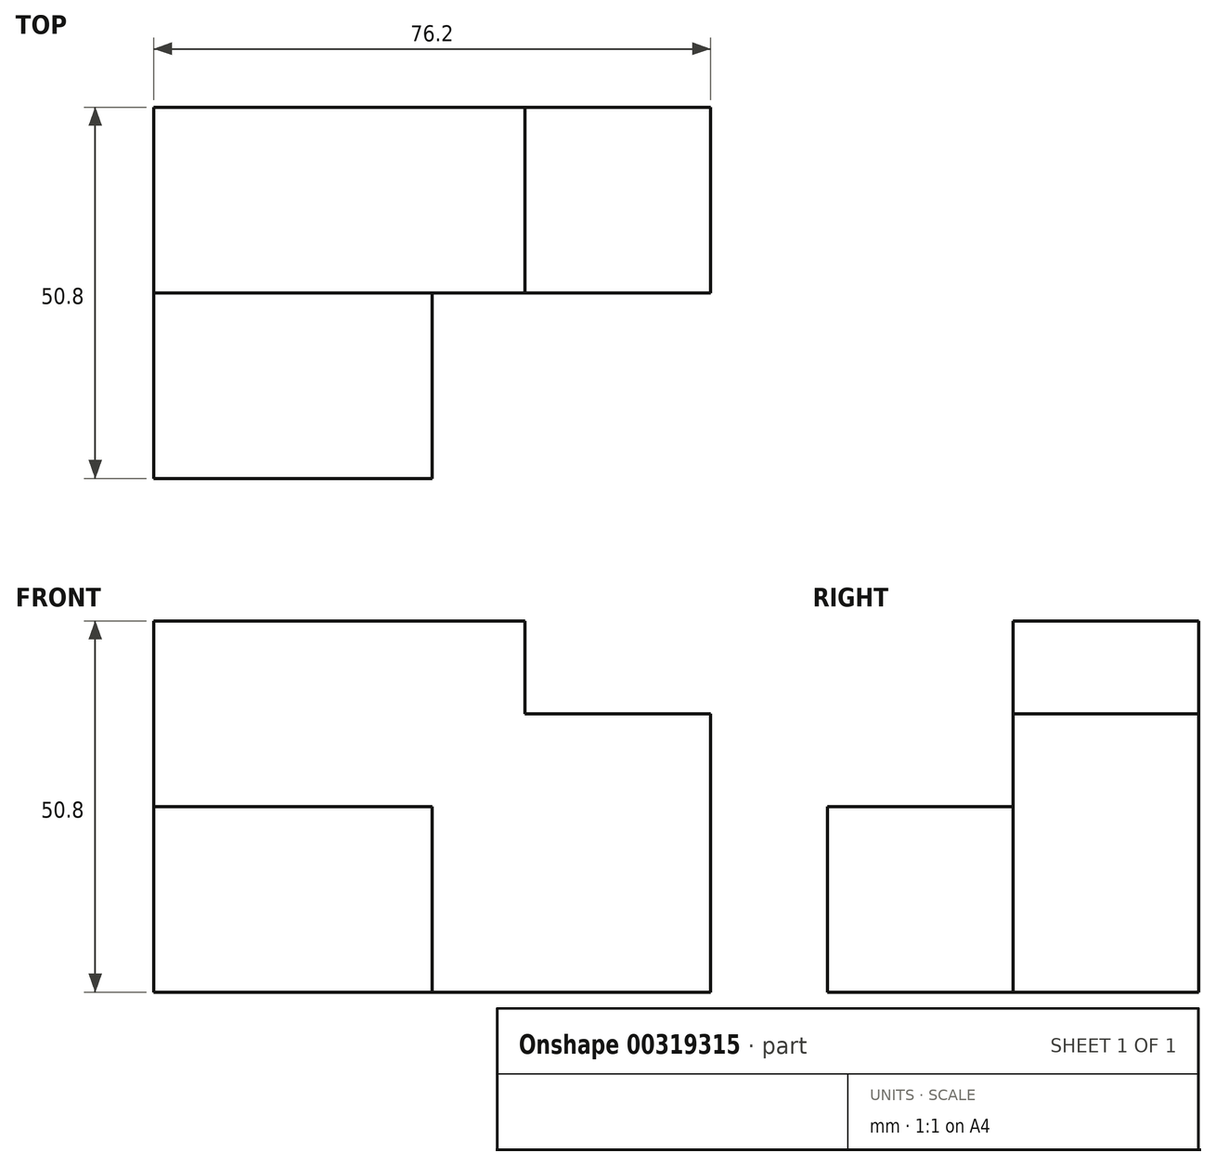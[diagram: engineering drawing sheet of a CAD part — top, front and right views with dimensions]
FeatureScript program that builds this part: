
annotation { "Feature Type Name" : "Feature", "Feature Type Description" : "" }
export const myFeature = defineFeature(function(context is Context, id is Id, definition is map)
    precondition{}
    {
        {
            var Q0;
            Q0=qCreatedBy(makeId("Top.planeOp"),FACE);
            var sketch = newSketch(context, id + "F0", { "sketchPlane" : qUnion([Q0])});
            skLineSegment(sketch, "E0", {"start": v(-44.14, -25.57) * mm, "end": v(32.06, -25.57) * mm});
            skLineSegment(sketch, "E1", {"start": v(32.06, -25.57) * mm, "end": v(32.06, -0.17) * mm});
            skLineSegment(sketch, "E2", {"start": v(32.06, -0.17) * mm, "end": v(-44.14, -0.17) * mm});
            skLineSegment(sketch, "E3", {"start": v(-44.14, -0.17) * mm, "end": v(-44.14, -25.57) * mm});
            skSolve(sketch);
        }
        {
            var Q0;
            Q0=makeQuery(id+"F0.imprint","IMPRINT",FACE,{"disambiguationData":[TD([[makeQuery(id+"F0.imprint","IMPRINT",EDGE,{"derivedFrom":sQuery(id+"F0.wireOp",EDGE,"E0")}),1.0]])]});
            extrude(context, id + "F1", {"entities" : qUnion([Q0]), "depth" : 38.1 * mm});
        }
        {
            var Q0;
            Q0=makeQuery(id+"F1.opExtrude","CAP_FACE",FACE,{"disambiguationData":[OSD([sQuery(id+"F0.wireOp",EDGE,"E0"),sQuery(id+"F0.wireOp",EDGE,"E1"),sQuery(id+"F0.wireOp",EDGE,"E2"),sQuery(id+"F0.wireOp",EDGE,"E3")])],"isStart":false});
            var sketch = newSketch(context, id + "F2", { "sketchPlane" : qUnion([Q0])});
            skLineSegment(sketch, "E4", {"start": v(-44.14, -0.17) * mm, "end": v(-44.14, -25.57) * mm});
            skLineSegment(sketch, "E5", {"start": v(-44.14, -25.57) * mm, "end": v(6.66, -25.57) * mm});
            skLineSegment(sketch, "E6", {"start": v(-44.14, -0.17) * mm, "end": v(6.66, -0.17) * mm});
            skLineSegment(sketch, "E7", {"start": v(6.66, -0.17) * mm, "end": v(6.66, -25.57) * mm});
            skSolve(sketch);
        }
        {
            var Q0;
            Q0=makeQuery(id+"F2.imprint","IMPRINT",FACE,{"disambiguationData":[TD([[makeQuery(id+"F2.imprint","IMPRINT",EDGE,{"derivedFrom":sQuery(id+"F2.wireOp",EDGE,"E4")}),1.0]])]});
            extrude(context, id + "F3", {"entities" : qUnion([Q0]), "operationType" : NewBodyOperationType.ADD, "depth" : 12.7 * mm});
        }
        {
            var Q0;
            Q0=makeQuery(id+"F3.boolean.opBoolean","MERGE",FACE,{"derivedFrom":[makeQuery(id+"F1.opExtrude","SWEPT_FACE",FACE,{"disambiguationData":[OSD([sQuery(id+"F0.wireOp",EDGE,"E0")])]}),makeQuery(id+"F3.opExtrude","SWEPT_FACE",FACE,{"disambiguationData":[OSD([sQuery(id+"F2.wireOp",EDGE,"E5")])]})]});
            var sketch = newSketch(context, id + "F4", { "sketchPlane" : qUnion([Q0])});
            skLineSegment(sketch, "E8", {"start": v(-44.14, 0) * mm, "end": v(-6.04, 0) * mm});
            skLineSegment(sketch, "E9", {"start": v(-6.04, 0) * mm, "end": v(-6.04, 25.4) * mm});
            skLineSegment(sketch, "E10", {"start": v(-6.04, 25.4) * mm, "end": v(-44.14, 25.4) * mm});
            skLineSegment(sketch, "E11", {"start": v(-44.14, 25.4) * mm, "end": v(-44.14, 0) * mm});
            skSolve(sketch);
        }
        {
            var Q0;
            Q0=makeQuery(id+"F4.imprint","IMPRINT",FACE,{"disambiguationData":[TD([[makeQuery(id+"F4.imprint","IMPRINT",EDGE,{"derivedFrom":sQuery(id+"F4.wireOp",EDGE,"E8")}),1.0]])]});
            extrude(context, id + "F5", {"entities" : qUnion([Q0]), "operationType" : NewBodyOperationType.ADD, "depth" : 25.4 * mm});
        }
    });
